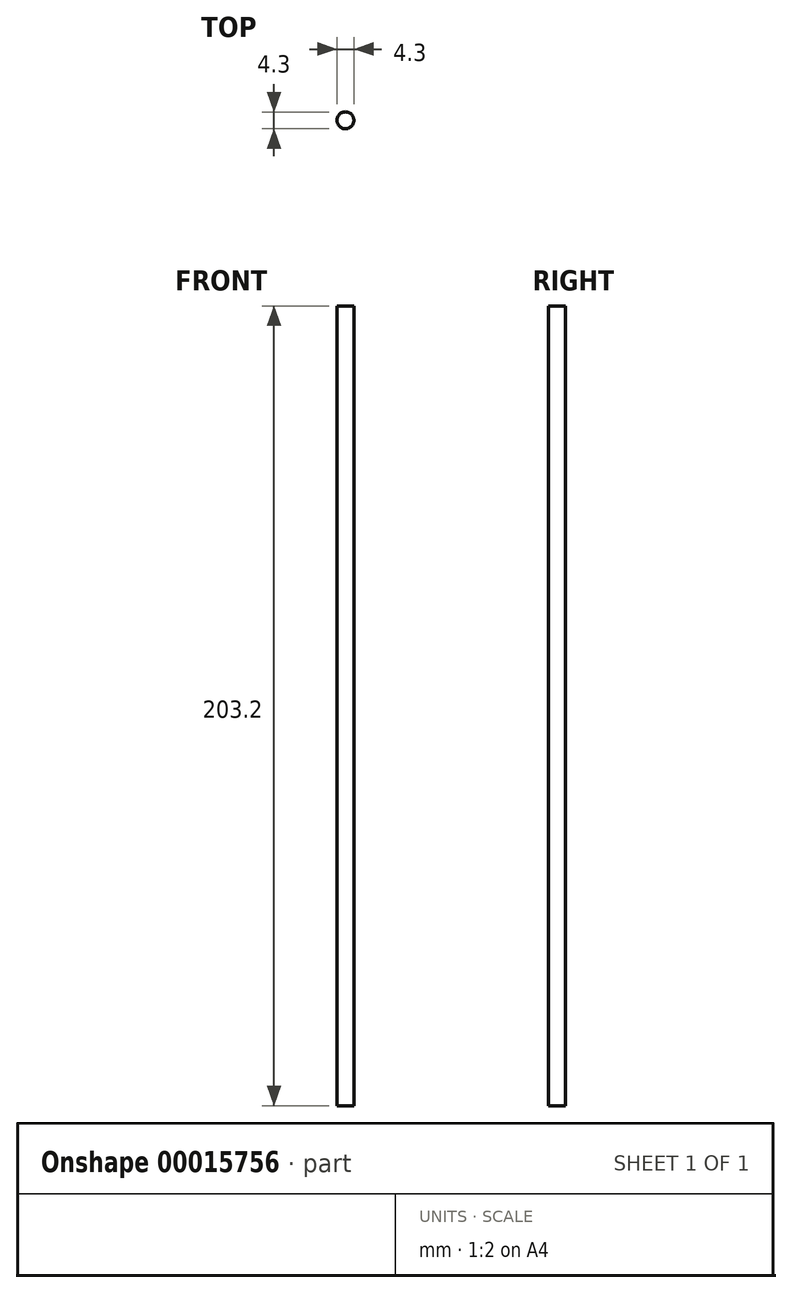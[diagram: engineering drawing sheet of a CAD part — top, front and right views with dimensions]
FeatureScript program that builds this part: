
annotation { "Feature Type Name" : "Feature", "Feature Type Description" : "" }
export const myFeature = defineFeature(function(context is Context, id is Id, definition is map)
    precondition{}
    {
        {
            var Q0;
            Q0=qCreatedBy(makeId("Top.planeOp"),FACE);
            var sketch = newSketch(context, id + "F0", { "sketchPlane" : qUnion([Q0])});
            skCircle(sketch, "E0", {"center": v(0, 0) * mm, "radius": 2.15 * mm});
            skSolve(sketch);
        }
        {
            var Q0;
            Q0 = qSketchRegion(id + "F0", true);
            extrude(context, id + "F1", {"entities" : qUnion([Q0]), "depth" : 203.2 * mm});
        }
    });
